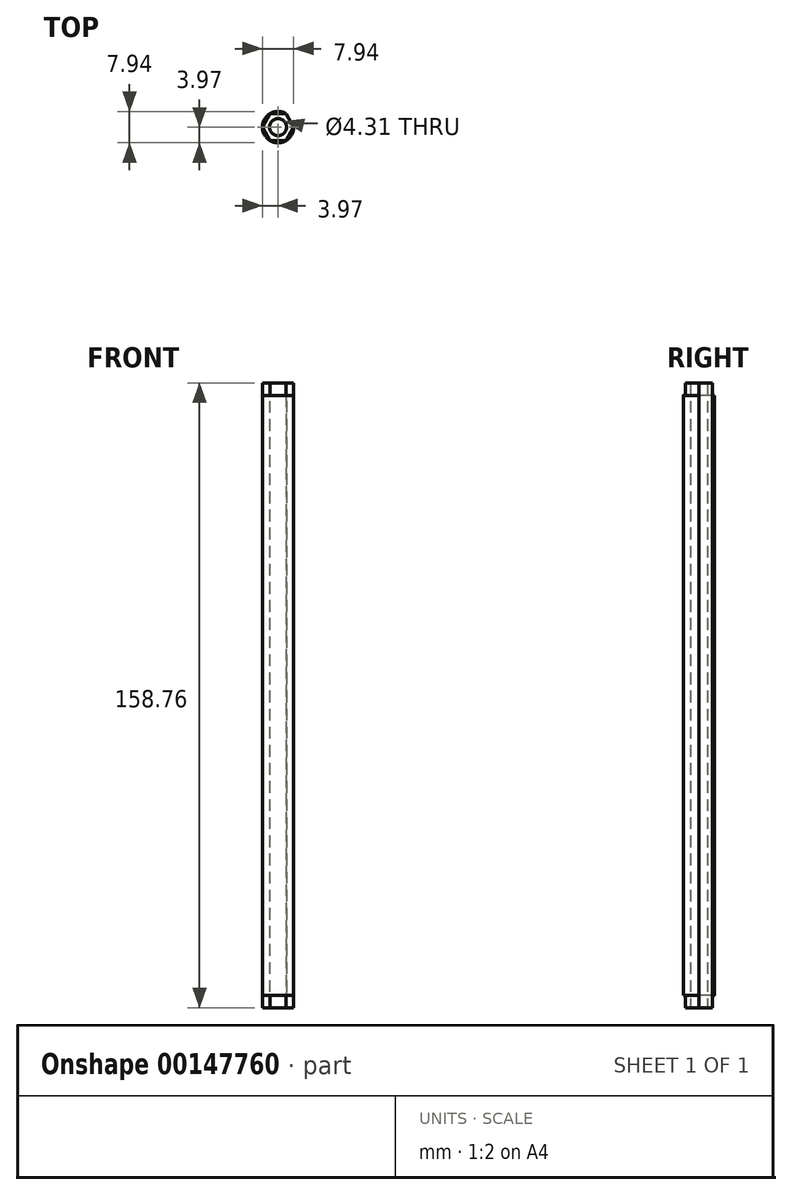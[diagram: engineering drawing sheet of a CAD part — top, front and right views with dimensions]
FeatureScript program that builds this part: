
annotation { "Feature Type Name" : "Feature", "Feature Type Description" : "" }
export const myFeature = defineFeature(function(context is Context, id is Id, definition is map)
    precondition{}
    {
        {
            var Q0;
            Q0=qCreatedBy(makeId("Top.planeOp"),FACE);
            var sketch = newSketch(context, id + "F0", { "sketchPlane" : qUnion([Q0])});
            skCircle(sketch, "E0", {"center": v(0, 0) * mm, "radius": 3.97 * mm});
            skCircle(sketch, "E1", {"center": v(0, 0) * mm, "radius": 2.15 * mm});
            skSolve(sketch);
        }
        {
            var Q0;
            Q0=qSketchRegion(id+"F0",true);
            extrude(context, id + "F1", {"entities" : qUnion([Q0]), "depth" : 152.4 * mm});
        }
        {
            var Q0;
            Q0=makeQuery(id+"F1.opExtrude","CAP_FACE",FACE,{"disambiguationData":[OSD([sQuery(id+"F0.wireOp",EDGE,"E0"),sQuery(id+"F0.wireOp",EDGE,"E1")])],"isStart":false});
            cPlane(context, id + "F2", {"entities" : qUnion([Q0]), "cplaneType" : CPlaneType.OFFSET, "offset" : 3.17 * mm, "width" : 152.4 * mm, "height" : 152.4 * mm});
        }
        {
            var Q0;
            Q0=makeQuery(id+"F1.opExtrude","CAP_FACE",FACE,{"disambiguationData":[OSD([sQuery(id+"F0.wireOp",EDGE,"E0"),sQuery(id+"F0.wireOp",EDGE,"E1")])],"isStart":true});
            var sketch = newSketch(context, id + "F3", { "sketchPlane" : qUnion([Q0])});
            skCircle(sketch, "E2.cCircle", {"center": v(0, 0) * mm, "radius": 3.97 * mm, "construction": true});
            skLineSegment(sketch, "E2.0", {"start": v(3.97, 0) * mm, "end": v(1.98, -3.44) * mm});
            skLineSegment(sketch, "E2.1", {"start": v(1.98, -3.44) * mm, "end": v(-1.98, -3.44) * mm});
            skLineSegment(sketch, "E2.2", {"start": v(-1.98, -3.44) * mm, "end": v(-3.97, 0) * mm});
            skLineSegment(sketch, "E2.3", {"start": v(-3.97, 0) * mm, "end": v(-1.98, 3.44) * mm});
            skLineSegment(sketch, "E2.4", {"start": v(-1.98, 3.44) * mm, "end": v(1.98, 3.44) * mm});
            skLineSegment(sketch, "E2.5", {"start": v(1.98, 3.44) * mm, "end": v(3.97, 0) * mm});
            skCircle(sketch, "E3", {"center": v(0, 0) * mm, "radius": 2.15 * mm});
            skSolve(sketch);
        }
        {
            var Q0;
            Q0=qSketchRegion(id+"F3",true);
            var Q1;
            Q1=qCreatedBy(id+"F2.planeOp",FACE);
            extrude(context, id + "F4", {"entities" : qUnion([Q0]), "operationType" : NewBodyOperationType.ADD, "depth" : 3.17 * mm, "hasSecondDirection" : true, "secondDirectionBound" : SecondDirectionBoundingType.UP_TO_SURFACE, "secondDirectionOppositeDirection" : true, "secondDirectionBoundEntityFace" : qUnion([Q1]), "secondDirectionDepth" : 25.4 * mm});
        }
        {
            var Q0;
            {var subQ0=sQuery(id+"F0.wireOp",EDGE,"E0");var subQ1=makeQuery(id+"F1.opExtrude","CAP_FACE",FACE,{"disambiguationData":[OSD([subQ0,sQuery(id+"F0.wireOp",EDGE,"E1")])],"isStart":true});Q0=makeQuery(id+"F4.boolean.opBoolean","SPLIT",FACE,{"disambiguationData":[TD([makeQuery(id+"F1.opExtrude","SWEPT_FACE",FACE,{"disambiguationData":[OSD([subQ0])]}),subQ1,makeQuery(id+"F4.opExtrude","SWEPT_FACE",FACE,{"disambiguationData":[OSD([sQuery(id+"F3.wireOp",EDGE,"E2.0")])]}),makeQuery(id+"F4.opExtrude","SWEPT_FACE",FACE,{"disambiguationData":[OSD([sQuery(id+"F3.wireOp",EDGE,"E2.1")])]}),makeQuery(id+"F4.opExtrude","SWEPT_FACE",FACE,{"disambiguationData":[OSD([sQuery(id+"F3.wireOp",EDGE,"E2.5")])]})])],"derivedFrom":subQ1});}
            var Q1;
            {var subQ0=sQuery(id+"F0.wireOp",EDGE,"E0");var subQ1=makeQuery(id+"F1.opExtrude","CAP_FACE",FACE,{"disambiguationData":[OSD([subQ0,sQuery(id+"F0.wireOp",EDGE,"E1")])],"isStart":false});Q1=makeQuery(id+"F4.boolean.opBoolean","SPLIT",FACE,{"disambiguationData":[TD([makeQuery(id+"F1.opExtrude","SWEPT_FACE",FACE,{"disambiguationData":[OSD([subQ0])]}),subQ1,makeQuery(id+"F4.opExtrude","SWEPT_FACE",FACE,{"disambiguationData":[OSD([sQuery(id+"F3.wireOp",EDGE,"E2.0")])]}),makeQuery(id+"F4.opExtrude","SWEPT_FACE",FACE,{"disambiguationData":[OSD([sQuery(id+"F3.wireOp",EDGE,"E2.1")])]}),makeQuery(id+"F4.opExtrude","SWEPT_FACE",FACE,{"disambiguationData":[OSD([sQuery(id+"F3.wireOp",EDGE,"E2.5")])]})])],"derivedFrom":subQ1});}
            extrude(context, id + "F5", {"entities" : qUnion([Q0]), "operationType" : NewBodyOperationType.REMOVE, "endBound" : BoundingType.UP_TO_SURFACE, "oppositeDirection" : true, "endBoundEntityFace" : qUnion([Q1]), "depth" : 25.4 * mm});
        }
    });
